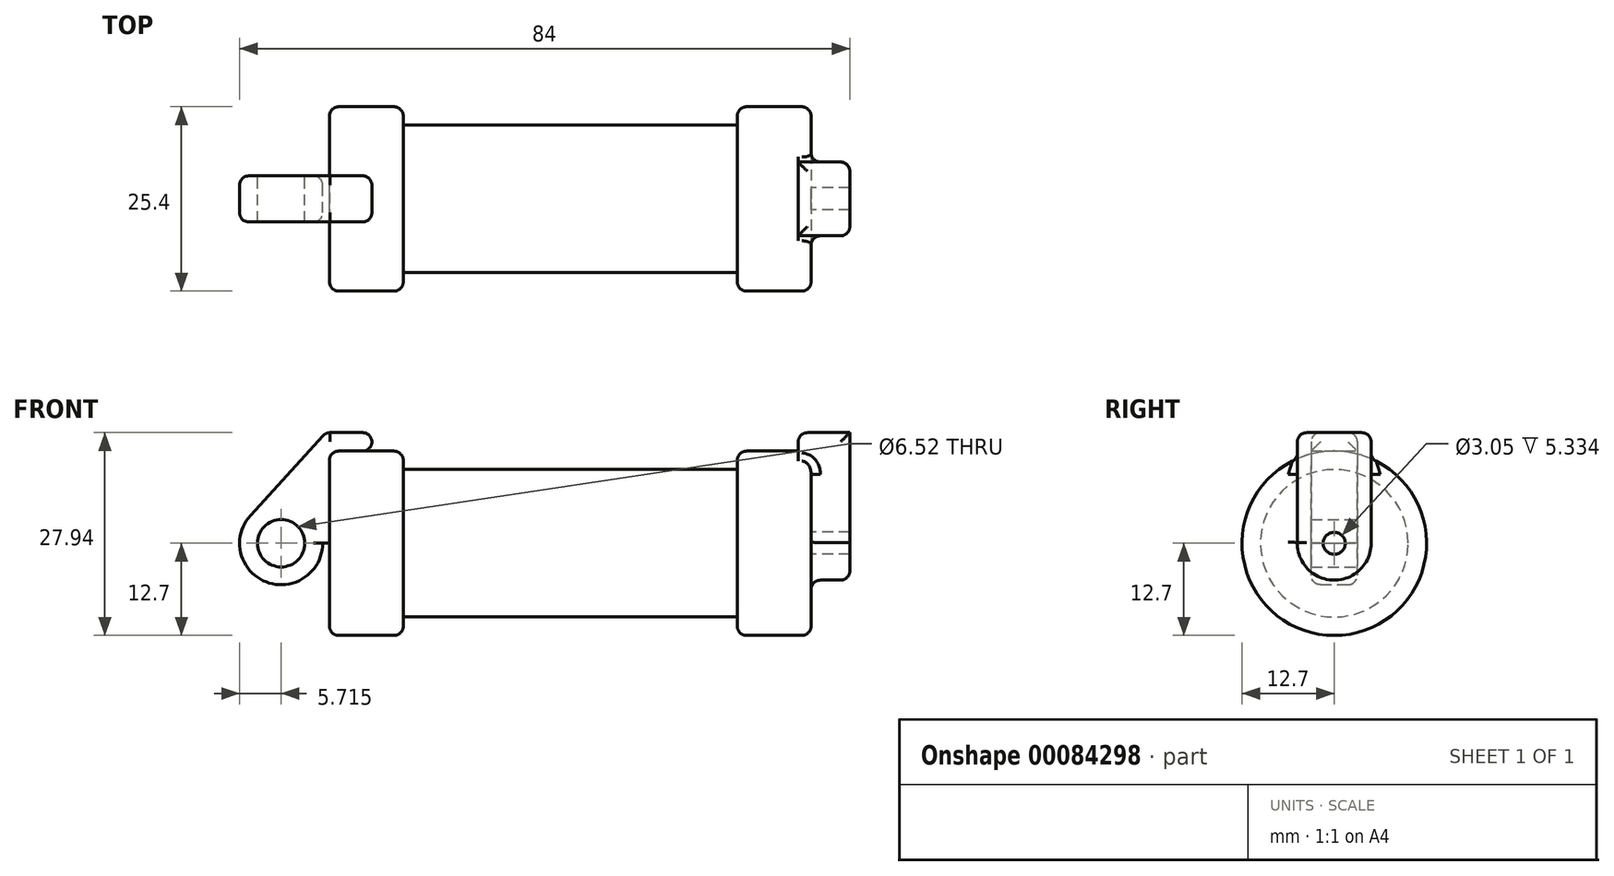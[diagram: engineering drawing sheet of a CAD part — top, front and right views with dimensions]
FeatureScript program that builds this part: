
annotation { "Feature Type Name" : "Feature", "Feature Type Description" : "" }
export const myFeature = defineFeature(function(context is Context, id is Id, definition is map)
    precondition{}
    {
        {
            var Q0;
            Q0=qCreatedBy(makeId("Front.planeOp"),FACE);
            var sketch = newSketch(context, id + "F0", { "sketchPlane" : qUnion([Q0])});
            skLineSegment(sketch, "E0", {"start": v(0, 0) * mm, "end": v(0, 12.7) * mm});
            skLineSegment(sketch, "E1", {"start": v(0, 12.7) * mm, "end": v(10.16, 12.7) * mm});
            skLineSegment(sketch, "E2", {"start": v(10.16, 12.7) * mm, "end": v(10.16, 10.16) * mm});
            skLineSegment(sketch, "E3", {"start": v(10.16, 10.16) * mm, "end": v(56.13, 10.16) * mm});
            skLineSegment(sketch, "E4", {"start": v(56.13, 10.16) * mm, "end": v(56.13, 12.7) * mm});
            skLineSegment(sketch, "E5", {"start": v(56.13, 12.7) * mm, "end": v(66.3, 12.7) * mm});
            skLineSegment(sketch, "E6", {"start": v(66.3, 12.7) * mm, "end": v(66.3, 0) * mm});
            skLineSegment(sketch, "E7", {"start": v(66.3, 0) * mm, "end": v(0, 0) * mm});
            skLineSegment(sketch, "E8", {"start": v(5.84, 15.24) * mm, "end": v(-0.5, 15.24) * mm});
            skLineSegment(sketch, "E9", {"start": v(-0.5, 15.24) * mm, "end": v(-10.88, 3.85) * mm});
            skLineSegment(sketch, "E10", {"start": v(0, 0) * mm, "end": v(-6.65, 0) * mm});
            skCircle(sketch, "E11", {"center": v(-6.65, 0) * mm, "radius": 5.72 * mm});
            skCircle(sketch, "E12", {"center": v(-6.65, 0) * mm, "radius": 3.18 * mm});
            skLineSegment(sketch, "E13", {"start": v(5.84, 15.24) * mm, "end": v(5.84, -9.4) * mm});
            skLineSegment(sketch, "E14", {"start": v(5.84, -9.4) * mm, "end": v(-8.18, -5.5) * mm});
            skSolve(sketch);
        }
        {
            var Q0;
            {var subQ0=sQuery(id+"F0.wireOp",EDGE,"E0");Q0=makeQuery(id+"F0.imprint","IMPRINT",FACE,{"disambiguationData":[TD([[makeQuery(id+"F0.imprint","IMPRINT",EDGE,{"derivedFrom":subQ0}),-1.0]])]});}
            var Q1;
            {var subQ0=sQuery(id+"F0.wireOp",EDGE,"E2");Q1=makeQuery(id+"F0.imprint","IMPRINT",FACE,{"disambiguationData":[TD([[makeQuery(id+"F0.imprint","IMPRINT",EDGE,{"derivedFrom":subQ0}),-1.0]])]});}
            var Q2;
            Q2=sQuery(id+"F0.wireOp",EDGE,"E7");
            revolve(context, id + "F1", {"entities" : qUnion([Q0, Q1]), "axis" : qUnion([Q2]), "revolveType" : RevolveType.FULL});
        }
        {
            var Q0;
            {var subQ3=sQuery(id+"F0.wireOp",EDGE,"E0");Q0=makeQuery(id+"F0.imprint","IMPRINT",FACE,{"disambiguationData":[TD([[makeQuery(id+"F0.imprint","IMPRINT",EDGE,{"derivedFrom":subQ3}),1.0]])]});}
            var Q1;
            {var subQ4=sQuery(id+"F0.wireOp",EDGE,"E12");Q1=makeQuery(id+"F0.imprint","IMPRINT",FACE,{"disambiguationData":[TD([[makeQuery(id+"F0.imprint","IMPRINT",EDGE,{"derivedFrom":subQ4}),-1.0]])]});}
            extrude(context, id + "F2", {"entities" : qUnion([Q0, Q1]), "endBound" : BoundingType.SYMMETRIC, "depth" : 6.35 * mm});
        }
        {
            var Q0;
            {var subQ0=sQuery(id+"F0.wireOp",EDGE,"E6");Q0=makeQuery(id+"F2.boolean.opBoolean","MERGE",FACE,{"derivedFrom":[makeQuery(id+"F1.opRevolve","SWEPT_FACE",FACE,{"disambiguationData":[OSD([subQ0])]}),makeQuery(id+"F2.opExtrude","SWEPT_FACE",FACE,{"disambiguationData":[OSD([subQ0])]})]});}
            var sketch = newSketch(context, id + "F3", { "sketchPlane" : qUnion([Q0])});
            skCircle(sketch, "E15", {"center": v(0, 0) * mm, "radius": 1.52 * mm});
            skCircle(sketch, "E16", {"center": v(0, 0) * mm, "radius": 5.08 * mm});
            skLineSegment(sketch, "E17", {"start": v(-5.08, -0.12) * mm, "end": v(-5.08, 15.24) * mm});
            skLineSegment(sketch, "E18", {"start": v(5.08, 0) * mm, "end": v(5.08, 15.24) * mm});
            skLineSegment(sketch, "E19", {"start": v(5.08, 15.24) * mm, "end": v(-5.08, 15.24) * mm});
            skSolve(sketch);
        }
        {
            var Q0;
            {var subQ0=sQuery(id+"F0.wireOp",EDGE,"E1");var subQ1=sQuery(id+"F0.wireOp",EDGE,"E2");var subQ2=sQuery(id+"F0.wireOp",EDGE,"E8");var subQ3=sQuery(id+"F0.wireOp",EDGE,"E14");var subQ4=sQuery(id+"F0.wireOp",EDGE,"E9");var subQ5=sQuery(id+"F0.wireOp",EDGE,"E11");var subQ6=sQuery(id+"F0.wireOp",EDGE,"E13");Q0=makeQuery(id+"F2.boolean.opBoolean","SPLIT",FACE,{"disambiguationData":[TD([makeQuery(id+"F1.opRevolve","SWEPT_FACE",FACE,{"disambiguationData":[OSD([sQuery(id+"F0.wireOp",EDGE,"E0")])]})])],"derivedFrom":makeQuery(id+"F2.opExtrude","CAP_FACE",FACE,{"disambiguationData":[OSD([subQ0,subQ1,sQuery(id+"F0.wireOp",EDGE,"E3"),sQuery(id+"F0.wireOp",EDGE,"E4"),sQuery(id+"F0.wireOp",EDGE,"E5"),sQuery(id+"F0.wireOp",EDGE,"E6"),sQuery(id+"F0.wireOp",EDGE,"E7"),subQ2,subQ4,subQ5,subQ6,subQ3])],"isStart":true})});}
            var sketch = newSketch(context, id + "F4", { "sketchPlane" : qUnion([Q0])});
            skCircle(sketch, "E20", {"center": v(6.65, 0) * mm, "radius": 3.26 * mm});
            skSolve(sketch);
        }
        {
            var Q0;
            Q0 = qSketchRegion(id + "F4", true);
            extrude(context, id + "F5", {"entities" : qUnion([Q0]), "operationType" : NewBodyOperationType.REMOVE, "oppositeDirection" : true, "depth" : 25.4 * mm});
        }
        {
            var Q0;
            {var subQ0=sQuery(id+"F3.wireOp",EDGE,"E19");Q0=makeQuery(id+"F3.imprint","IMPRINT",FACE,{"disambiguationData":[TD([[makeQuery(id+"F3.imprint","IMPRINT",EDGE,{"derivedFrom":subQ0}),1.0]])]});}
            extrude(context, id + "F6", {"entities" : qUnion([Q0]), "operationType" : NewBodyOperationType.ADD, "oppositeDirection" : true, "depth" : 1.78 * mm});
        }
        {
            var Q0;
            Q0 = qSketchRegion(id + "F3", true);
            extrude(context, id + "F7", {"entities" : qUnion([Q0]), "operationType" : NewBodyOperationType.ADD, "depth" : 5.33 * mm});
        }
        {
            var Q0;
            Q0=makeQuery(id+"F1.opRevolve","SWEPT_EDGE",EDGE,{"disambiguationData":[OSD([sQuery(id+"F0.wireOp",EDGE,"E0"),sQuery(id+"F0.wireOp",EDGE,"E1")])]});
            var Q1;
            Q1=makeQuery(id+"F1.opRevolve","SWEPT_EDGE",EDGE,{"disambiguationData":[OSD([sQuery(id+"F0.wireOp",EDGE,"E1"),sQuery(id+"F0.wireOp",EDGE,"E2")])]});
            var Q2;
            Q2=makeQuery(id+"F1.opRevolve","SWEPT_EDGE",EDGE,{"disambiguationData":[OSD([sQuery(id+"F0.wireOp",EDGE,"E4"),sQuery(id+"F0.wireOp",EDGE,"E5")])]});
            var Q3;
            {var subQ0=sQuery(id+"F3.wireOp",EDGE,"E18");var subQ1=sQuery(id+"F3.wireOp",EDGE,"E17");var subQ2=sQuery(id+"F0.wireOp",EDGE,"E6");var subQ3=sQuery(id+"F0.wireOp",EDGE,"E5");Q3=makeQuery(id+"FmkUibtV5aABIfZ_1.boolean.opBoolean","SPLIT",EDGE,{"disambiguationData":[TD([makeQuery(id+"F1.opRevolve","SWEPT_FACE",FACE,{"disambiguationData":[OSD([subQ3])]}),makeQuery(id+"F1.opRevolve","SWEPT_FACE",FACE,{"disambiguationData":[OSD([subQ2])]}),makeQuery(id+"F2.opExtrude","SWEPT_FACE",FACE,{"disambiguationData":[OSD([subQ2])]}),makeQuery(id+"FmkUibtV5aABIfZ_1.opExtrude","CAP_FACE",FACE,{"disambiguationData":[OSD([sQuery(id+"F3.wireOp",EDGE,"E15"),sQuery(id+"F3.wireOp",EDGE,"E16"),subQ1,subQ0,sQuery(id+"F3.wireOp",EDGE,"E19")])],"isStart":true}),makeQuery(id+"FmkUibtV5aABIfZ_1.opExtrude","SWEPT_FACE",FACE,{"disambiguationData":[OSD([subQ1])]}),makeQuery(id+"FmkUibtV5aABIfZ_1.opExtrude","SWEPT_FACE",FACE,{"disambiguationData":[OSD([subQ0])]})])],"derivedFrom":makeQuery(id+"F1.opRevolve","SWEPT_EDGE",EDGE,{"disambiguationData":[OSD([subQ3,subQ2])]})});}
            fillet(context, id + "F8", {"entities" : qUnion([Q0, Q1, Q2, Q3]), "radius" : 1.27 * mm, "tangentPropagation" : true, "allowEdgeOverflow" : false});
        }
        {
            var Q0;
            Q0=makeQuery(id+"F2.opExtrude","CAP_EDGE",EDGE,{"disambiguationData":[OSD([sQuery(id+"F0.wireOp",EDGE,"E8")])],"isStart":false});
            var Q1;
            Q1=makeQuery(id+"F2.opExtrude","CAP_EDGE",EDGE,{"disambiguationData":[OSD([sQuery(id+"F0.wireOp",EDGE,"E8")])],"isStart":true});
            var Q2;
            {var subQ0=sQuery(id+"F3.wireOp",EDGE,"E19");var subQ1=sQuery(id+"F3.wireOp",EDGE,"E17");Q2=makeQuery(id+"FnZKnojdGbRZ0yr_1.boolean.opBoolean","MERGE",EDGE,{"derivedFrom":[makeQuery(id+"FmkUibtV5aABIfZ_1.opExtrude","SWEPT_EDGE",EDGE,{"disambiguationData":[OSD([subQ1,subQ0])]}),makeQuery(id+"FnZKnojdGbRZ0yr_1.opExtrude","SWEPT_EDGE",EDGE,{"disambiguationData":[OSD([subQ1,subQ0])]})]});}
            var Q3;
            Q3=makeQuery(id+"FnZKnojdGbRZ0yr_1.opExtrude","CAP_EDGE",EDGE,{"disambiguationData":[OSD([sQuery(id+"F3.wireOp",EDGE,"E19")])],"isStart":false});
            fillet(context, id + "F9", {"entities" : qUnion([Q0, Q1, Q2, Q3]), "radius" : 1.27 * mm, "tangentPropagation" : true, "allowEdgeOverflow" : false});
        }
        {
            var Q0;
            Q0=makeQuery(id+"F2.opExtrude","CAP_EDGE",EDGE,{"disambiguationData":[OSD([sQuery(id+"F0.wireOp",EDGE,"E9")])],"isStart":false});
            var Q1;
            Q1=makeQuery(id+"F2.opExtrude","SWEPT_EDGE",EDGE,{"disambiguationData":[OSD([sQuery(id+"F0.wireOp",EDGE,"E8"),sQuery(id+"F0.wireOp",EDGE,"E13")])]});
            var Q2;
            {var subQ0=sQuery(id+"F0.wireOp",EDGE,"E2");Q2=makeQuery(id+"F8.opFillet","BLEND_EDGE",EDGE,{"blendedFrom":[makeQuery(id+"F1.opRevolve","SWEPT_EDGE",EDGE,{"disambiguationData":[OSD([sQuery(id+"F0.wireOp",EDGE,"E1"),subQ0])]}),makeQuery(id+"F1.opRevolve","SWEPT_FACE",FACE,{"disambiguationData":[OSD([subQ0])]})],"blendedInto":[makeQuery(id+"F1.opRevolve","SWEPT_FACE",FACE,{"disambiguationData":[OSD([subQ0])]})]});}
            var Q3;
            Q3=makeQuery(id+"F2.opExtrude","SWEPT_EDGE",EDGE,{"disambiguationData":[OSD([sQuery(id+"F0.wireOp",EDGE,"E0"),sQuery(id+"F0.wireOp",EDGE,"E1")])]});
            var Q4;
            {var subQ0=sQuery(id+"F3.wireOp",EDGE,"E19");var subQ1=sQuery(id+"F3.wireOp",EDGE,"E17");Q4=makeQuery(id+"F7.boolean.opBoolean","MERGE",EDGE,{"derivedFrom":[makeQuery(id+"F6.opExtrude","SWEPT_EDGE",EDGE,{"disambiguationData":[OSD([subQ1,subQ0])]}),makeQuery(id+"F7.opExtrude","SWEPT_EDGE",EDGE,{"disambiguationData":[OSD([subQ1,subQ0])]})]});}
            var Q5;
            {var subQ0=sQuery(id+"F3.wireOp",EDGE,"E19");var subQ1=sQuery(id+"F3.wireOp",EDGE,"E18");Q5=makeQuery(id+"F7.boolean.opBoolean","MERGE",EDGE,{"derivedFrom":[makeQuery(id+"F6.opExtrude","SWEPT_EDGE",EDGE,{"disambiguationData":[OSD([subQ1,subQ0])]}),makeQuery(id+"F7.opExtrude","SWEPT_EDGE",EDGE,{"disambiguationData":[OSD([subQ1,subQ0])]})]});}
            var Q6;
            Q6=makeQuery(id+"F6.opExtrude","CAP_EDGE",EDGE,{"disambiguationData":[OSD([sQuery(id+"F3.wireOp",EDGE,"E19")])],"isStart":false});
            var Q7;
            Q7=makeQuery(id+"F2.opExtrude","SWEPT_EDGE",EDGE,{"disambiguationData":[OSD([sQuery(id+"F0.wireOp",EDGE,"E1"),sQuery(id+"F0.wireOp",EDGE,"E13")])]});
            var Q8;
            Q8=makeQuery(id+"F7.opExtrude","CAP_EDGE",EDGE,{"disambiguationData":[OSD([sQuery(id+"F3.wireOp",EDGE,"E18")])],"isStart":false});
            var Q9;
            Q9=makeQuery(id+"F7.opExtrude","CAP_EDGE",EDGE,{"disambiguationData":[OSD([sQuery(id+"F3.wireOp",EDGE,"E17")])],"isStart":true});
            var Q10;
            Q10=makeQuery(id+"F7.opExtrude","CAP_EDGE",EDGE,{"disambiguationData":[OSD([sQuery(id+"F3.wireOp",EDGE,"E18")])],"isStart":true});
            fillet(context, id + "F10", {"entities" : qUnion([Q0, Q1, Q2, Q3, Q4, Q5, Q6, Q7, Q8, Q9, Q10]), "radius" : 1.27 * mm, "tangentPropagation" : true, "allowEdgeOverflow" : false});
        }
    });
